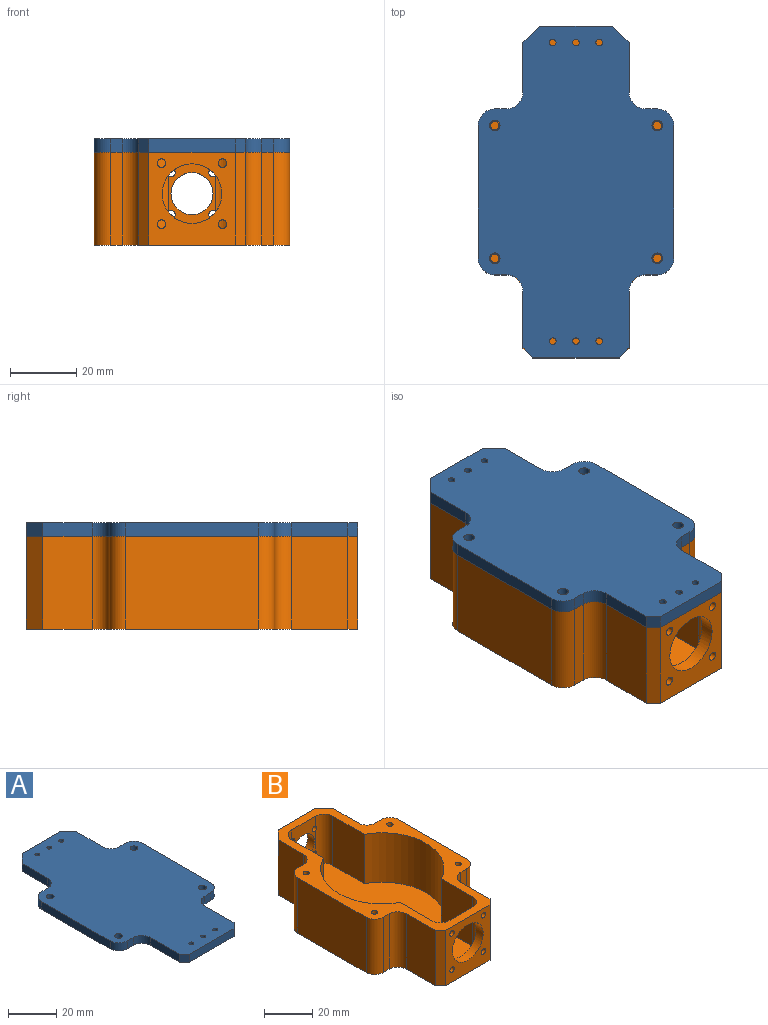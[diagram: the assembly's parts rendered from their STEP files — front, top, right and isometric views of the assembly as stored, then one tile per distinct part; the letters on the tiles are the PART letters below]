
ASSEMBLY  parts=2 mates=1
PART A: 36 faces, bbox 59x100x4 mm
  f0: plane 100x59mm, normal (0,0,1), area 4465mm2, adj f2,f3,f4,f5,f6,f7,f8,f9
  f1: plane 100x59mm, normal (0,0,-1), area 4465mm2, adj f2,f3,f4,f5,f6,f7,f8,f9
  f2: plane 26x4mm, normal (0,-1,0), area 104mm2, adj f0,f1,f16,f17
  f3: plane 17x4mm, normal (1,0,0), area 68mm2, adj f0,f1,f17,f18
  f4: plane 4x3.5mm, normal (0,-1,0), area 14mm2, adj f0,f1,f18,f19
  f5: plane 40x4mm, normal (1,0,0), area 160mm2, adj f0,f1,f19,f20
  f6: plane 4x3.5mm, normal (0,1,0), area 14mm2, adj f0,f1,f20,f21
  f7: plane 15x4mm, normal (1,0,0), area 60mm2, adj f0,f1,f14,f21
  f8: plane 22x4mm, normal (0,1,0), area 88mm2, adj f0,f1,f14,f15
  f9: plane 15x4mm, normal (-1,0,0), area 60mm2, adj f0,f1,f15,f22
  f10: plane 4x3.5mm, normal (0,1,0), area 14mm2, adj f0,f1,f22,f23
  f11: plane 40x4mm, normal (-1,0,0), area 160mm2, adj f0,f1,f23,f24
  f12: plane 4x3.5mm, normal (0,-1,0), area 14mm2, adj f0,f1,f24,f25
  f13: plane 17x4mm, normal (-1,0,0), area 68mm2, adj f0,f1,f16,f25
  f14: plane 5x5mm, normal (0.71,0.71,0), area 28.3mm2, adj f0,f1,f7,f8
  f15: plane 5x5mm, normal (-0.71,0.71,0), area 28.3mm2, adj f0,f1,f8,f9
  f16: plane 4x3mm, normal (-0.71,-0.71,0), area 17mm2, adj f0,f1,f2,f13
  f17: plane 4x3mm, normal (0.71,-0.71,0), area 17mm2, adj f0,f1,f2,f3
  f18: cylinder r=5mm len=5mm, axis (0,0,-1), area 31.4mm2, adj f0,f1,f3,f4
  f19: cylinder r=5mm len=5mm, axis (0,0,1), area 31.4mm2, adj f0,f1,f4,f5
  f20: cylinder r=5mm len=5mm, axis (0,0,-1), area 31.4mm2, adj f0,f1,f5,f6
  f21: cylinder r=5mm len=5mm, axis (0,0,-1), area 31.4mm2, adj f0,f1,f6,f7
  f22: cylinder r=5mm len=5mm, axis (0,0,1), area 31.4mm2, adj f0,f1,f9,f10
  f23: cylinder r=5mm len=5mm, axis (0,0,1), area 31.4mm2, adj f0,f1,f10,f11
  f24: cylinder r=5mm len=5mm, axis (0,0,-1), area 31.4mm2, adj f0,f1,f11,f12
  f25: cylinder r=5mm len=5mm, axis (0,0,1), area 31.4mm2, adj f0,f1,f12,f13
  f26: cylinder r=1.6mm len=4mm, axis (0,0,1), area 40.2mm2, adj f0,f1
  f27: cylinder r=1.6mm len=4mm, axis (0,0,1), area 40.2mm2, adj f0,f1
  f28: cylinder r=1.6mm len=4mm, axis (0,0,1), area 40.2mm2, adj f0,f1
  f29: cylinder r=1.6mm len=4mm, axis (0,0,1), area 40.2mm2, adj f0,f1
  f30: cylinder r=1mm len=4mm, axis (0,0,1), area 25.1mm2, adj f0,f1
  f31: cylinder r=1mm len=4mm, axis (0,0,1), area 25.1mm2, adj f0,f1
  f32: cylinder r=1mm len=4mm, axis (0,0,1), area 25.1mm2, adj f0,f1
  f33: cylinder r=1mm len=4mm, axis (0,0,1), area 25.1mm2, adj f0,f1
  f34: cylinder r=1mm len=4mm, axis (0,0,1), area 25.1mm2, adj f0,f1
  f35: cylinder r=1mm len=4mm, axis (0,0,1), area 25.1mm2, adj f0,f1
PART B: 59 faces, bbox 59x100x28 mm
  f0: plane 14x6.84mm, normal (0,1,0), area 63.2mm2, adj f23,f26,f27,f28
  f1: plane 28x26mm, normal (0,-1,0), area 452.3mm2, adj f13,f14,f28,f29,f30,f31,f32,f40
  f2: plane 28x17mm, normal (1,0,0), area 476mm2, adj f13,f14,f41,f42
  f3: plane 28x3.5mm, normal (0,-1,0), area 98mm2, adj f13,f14,f42,f43
  f4: plane 40x28mm, normal (1,0,0), area 1120mm2, adj f13,f14,f43,f44
  f5: plane 28x3.5mm, normal (0,1,0), area 98mm2, adj f13,f14,f44,f45
  f6: plane 28x15mm, normal (1,0,0), area 420mm2, adj f13,f14,f38,f45
  f7: plane 28x22mm, normal (0,1,0), area 468.1mm2, adj f13,f14,f33,f34,f35,f36,f37,f38
  f8: plane 28x15mm, normal (-1,0,0), area 420mm2, adj f13,f14,f39,f46
  f9: plane 28x3.5mm, normal (0,1,0), area 98mm2, adj f13,f14,f46,f47
  f10: plane 40x28mm, normal (-1,0,0), area 1120mm2, adj f13,f14,f47,f48
  f11: plane 28x3.5mm, normal (0,-1,0), area 98mm2, adj f13,f14,f48,f49
  f12: plane 28x17mm, normal (-1,0,0), area 476mm2, adj f13,f14,f40,f49
  f13: plane 100x59mm, normal (0,0,1), area 1442.6mm2, adj f1,f2,f3,f4,f5,f6,f7,f8
  f14: plane 100x59mm, normal (0,0,-1), area 4503.4mm2, adj f1,f2,f3,f4,f5,f6,f7,f8
  f15: cylinder r=25.5mm len=45mm, axis (0,0,1), area 1378.1mm2, adj f13,f16,f22,f23
  f16: plane 25x18.5mm, normal (1,0,0), area 462.5mm2, adj f13,f15,f23,f26
  f17: plane 14x6.84mm, normal (0,1,0), area 63.2mm2, adj f13,f26,f27,f28
  f18: plane 25x18.5mm, normal (-1,0,0), area 462.5mm2, adj f13,f19,f23,f27
  f19: cylinder r=25.5mm len=45mm, axis (0,0,1), area 1378.1mm2, adj f13,f18,f20,f23
  f20: plane 25x18.5mm, normal (-1,0,0), area 462.5mm2, adj f13,f19,f23,f24
  f21: plane 25x14mm, normal (0,-1,0), area 206.2mm2, adj f13,f23,f24,f25,f33,f34,f35,f36
  f22: plane 25x18.5mm, normal (1,0,0), area 462.5mm2, adj f13,f15,f23,f25
  f23: plane 92x51mm, normal (0,0,1), area 3039.6mm2, adj f0,f15,f16,f18,f19,f20,f21,f22
  f24: cylinder r=5mm len=25mm, axis (0,0,-1), area 194.3mm2, adj f13,f20,f21,f23,f35,f36
  f25: cylinder r=5mm len=25mm, axis (0,0,-1), area 194.3mm2, adj f13,f21,f22,f23,f33,f34
  f26: cylinder r=5mm len=25mm, axis (0,0,-1), area 168.5mm2, adj f0,f13,f16,f17,f23,f28,f31,f32
  f27: cylinder r=5mm len=25mm, axis (0,0,-1), area 168.5mm2, adj f0,f13,f17,f18,f23,f28,f29,f30
  f28: cylinder r=9mm len=18mm, axis (0,-1,0), area 231.5mm2, adj f0,f1,f17,f26,f27
  f29: cylinder r=1.3mm len=5.42mm, axis (0,-1,0), area 37.8mm2, adj f1,f27
  f30: cylinder r=1.3mm len=5.42mm, axis (0,-1,0), area 37.8mm2, adj f1,f27
  f31: cylinder r=1.3mm len=5.42mm, axis (0,-1,0), area 37.8mm2, adj f1,f26
  f32: cylinder r=1.3mm len=5.42mm, axis (0,-1,0), area 37.8mm2, adj f1,f26
  f33: cylinder r=1.3mm len=4mm, axis (0,1,0), area 32.7mm2, adj f7,f21,f25
  f34: cylinder r=1.3mm len=4mm, axis (0,1,0), area 32.7mm2, adj f7,f21,f25
  f35: cylinder r=1.3mm len=4mm, axis (0,1,0), area 32.7mm2, adj f7,f21,f24
  f36: cylinder r=1.3mm len=4mm, axis (0,1,0), area 32.7mm2, adj f7,f21,f24
  f37: cylinder r=6.35mm len=12.7mm, axis (0,1,0), area 159.6mm2, adj f7,f21
  f38: plane 28x5mm, normal (0.71,0.71,0), area 198mm2, adj f6,f7,f13,f14
  f39: plane 28x5mm, normal (-0.71,0.71,0), area 198mm2, adj f7,f8,f13,f14
  f40: plane 28x3mm, normal (-0.71,-0.71,0), area 118.8mm2, adj f1,f12,f13,f14
  f41: plane 28x3mm, normal (0.71,-0.71,0), area 118.8mm2, adj f1,f2,f13,f14
  f42: cylinder r=5mm len=28mm, axis (0,0,-1), area 219.9mm2, adj f2,f3,f13,f14
  f43: cylinder r=5mm len=28mm, axis (0,0,1), area 219.9mm2, adj f3,f4,f13,f14
  f44: cylinder r=5mm len=28mm, axis (0,0,-1), area 219.9mm2, adj f4,f5,f13,f14
  f45: cylinder r=5mm len=28mm, axis (0,0,-1), area 219.9mm2, adj f5,f6,f13,f14
  f46: cylinder r=5mm len=28mm, axis (0,0,1), area 219.9mm2, adj f8,f9,f13,f14
  f47: cylinder r=5mm len=28mm, axis (0,0,1), area 219.9mm2, adj f9,f10,f13,f14
  f48: cylinder r=5mm len=28mm, axis (0,0,-1), area 219.9mm2, adj f10,f11,f13,f14
  f49: cylinder r=5mm len=28mm, axis (0,0,1), area 219.9mm2, adj f11,f12,f13,f14
  f50: cylinder r=1.3mm len=25mm, axis (0,0,1), area 204.2mm2, adj f13,f51
  f51: plane 2.6x2.6mm, normal (0,0,1), area 5.3mm2, adj f50
  f52: cylinder r=1.3mm len=25mm, axis (0,0,1), area 204.2mm2, adj f13,f53
  f53: plane 2.6x2.6mm, normal (0,0,1), area 5.3mm2, adj f52
  f54: cylinder r=1.3mm len=25mm, axis (0,0,1), area 204.2mm2, adj f13,f55
  f55: plane 2.6x2.6mm, normal (0,0,1), area 5.3mm2, adj f54
  f56: cylinder r=1.3mm len=25mm, axis (0,0,1), area 204.2mm2, adj f13,f57
  f57: plane 2.6x2.6mm, normal (0,0,1), area 5.3mm2, adj f56
  f58: cylinder r=2mm len=4mm, axis (0,0,1), area 37.7mm2, adj f14,f23
PLACE A t=(0,0,28)mm
PLACE B at identity
MATE cylindrical A.f24 <-> B.f48  axis (0,0,-1) through (-24.5,-20,28)mm
